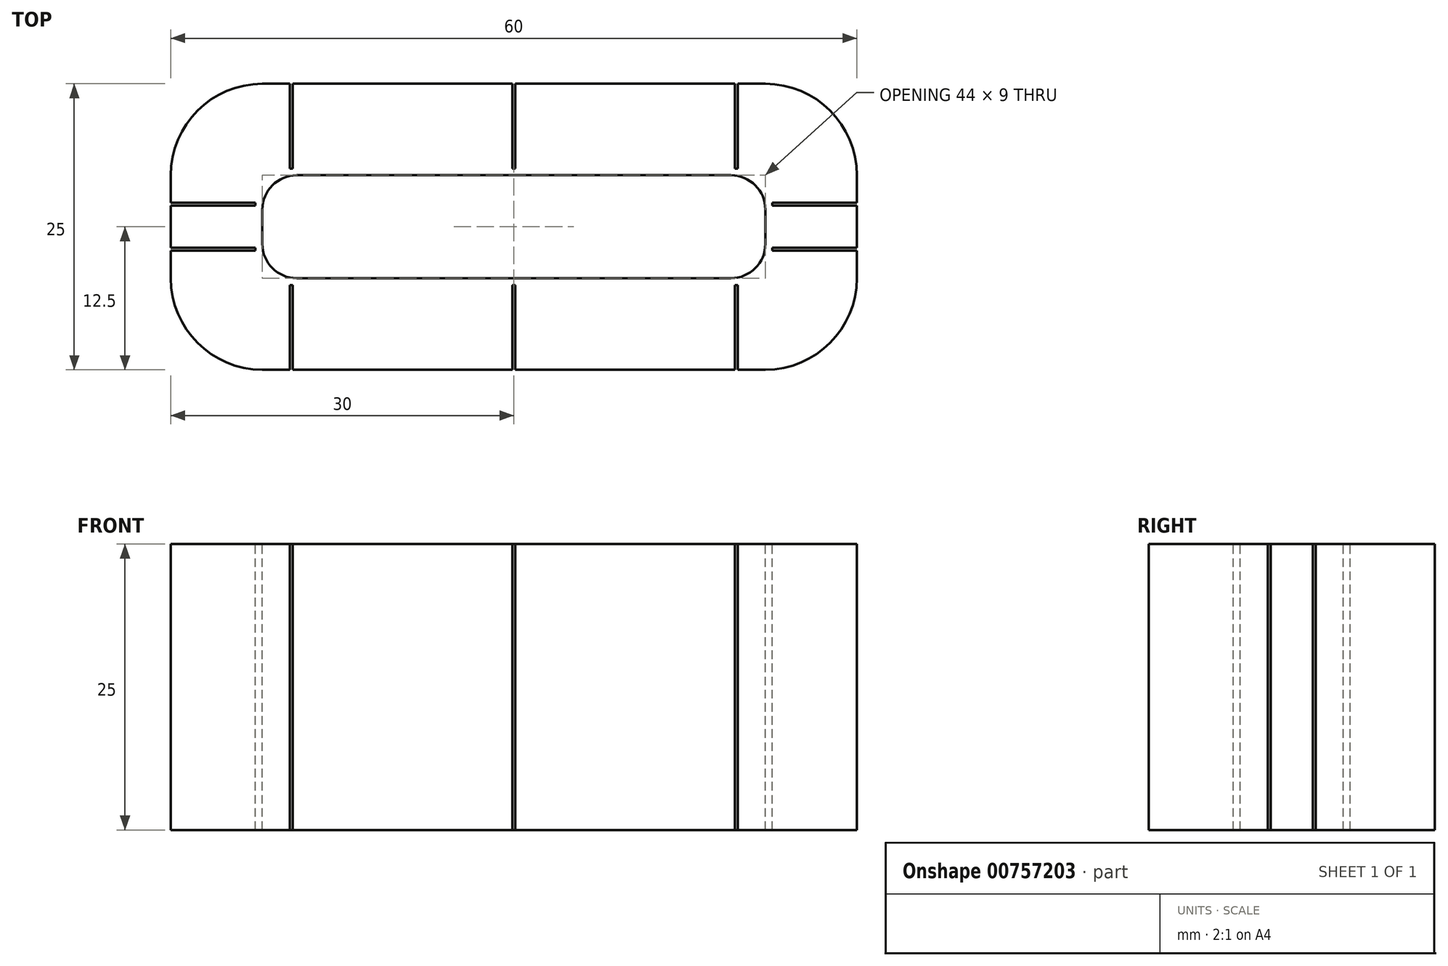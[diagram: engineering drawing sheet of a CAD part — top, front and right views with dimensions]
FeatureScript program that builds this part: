
annotation { "Feature Type Name" : "Feature", "Feature Type Description" : "" }
export const myFeature = defineFeature(function(context is Context, id is Id, definition is map)
    precondition{}
    {
        {
            var Q0;
            Q0=qCreatedBy(makeId("Top.planeOp"),FACE);
            var sketch = newSketch(context, id + "F0", { "sketchPlane" : qUnion([Q0])});
            skLineSegment(sketch, "E0.bottom", {"start": v(22, 12.5) * mm, "end": v(-22, 12.5) * mm});
            skLineSegment(sketch, "E0.top", {"start": v(22, -12.5) * mm, "end": v(-22, -12.5) * mm});
            skLineSegment(sketch, "E0.left", {"start": v(30, 4.5) * mm, "end": v(30, -4.5) * mm});
            skLineSegment(sketch, "E0.right", {"start": v(-30, 4.5) * mm, "end": v(-30, -4.5) * mm});
            skPoint(sketch, "E0.middle", {"position": v(0, 0) * mm});
            skPoint(sketch, "E1.visualSharp", {"position": v(-30, 12.5) * mm});
            skArc(sketch, "E1.filletArc", {"start": v(-22, 12.5) * mm, "mid": v(-27.66, 10.16) * mm, "end": v(-30, 4.5) * mm});
            skPoint(sketch, "E2.visualSharp", {"position": v(30, 12.5) * mm});
            skArc(sketch, "E2.filletArc", {"start": v(30, 4.5) * mm, "mid": v(27.66, 10.16) * mm, "end": v(22, 12.5) * mm});
            skPoint(sketch, "E3.visualSharp", {"position": v(30, -12.5) * mm});
            skArc(sketch, "E3.filletArc", {"start": v(22, -12.5) * mm, "mid": v(27.66, -10.16) * mm, "end": v(30, -4.5) * mm});
            skPoint(sketch, "E4.visualSharp", {"position": v(-30, -12.5) * mm});
            skArc(sketch, "E4.filletArc", {"start": v(-30, -4.5) * mm, "mid": v(-27.66, -10.16) * mm, "end": v(-22, -12.5) * mm});
            skSolve(sketch);
        }
        {
            var Q0;
            Q0 = qSketchRegion(id + "F0", true);
            extrude(context, id + "F1", {"entities" : qUnion([Q0]), "depth" : 25 * mm, "offsetDistance" : 25 * mm});
        }
        {
            var Q0;
            Q0=makeQuery(id+"F1.opExtrude","CAP_FACE",FACE,{"disambiguationData":[OSD([sQuery(id+"F0.wireOp",EDGE,"E0.bottom"),sQuery(id+"F0.wireOp",EDGE,"E0.top"),sQuery(id+"F0.wireOp",EDGE,"E0.left"),sQuery(id+"F0.wireOp",EDGE,"E0.right"),sQuery(id+"F0.wireOp",EDGE,"E1.filletArc"),sQuery(id+"F0.wireOp",EDGE,"E2.filletArc"),sQuery(id+"F0.wireOp",EDGE,"E3.filletArc"),sQuery(id+"F0.wireOp",EDGE,"E4.filletArc")])],"isStart":false});
            var sketch = newSketch(context, id + "F2", { "sketchPlane" : qUnion([Q0])});
            skLineSegment(sketch, "E5.bottom", {"start": v(19, 4.5) * mm, "end": v(-19, 4.5) * mm});
            skLineSegment(sketch, "E5.top", {"start": v(19, -4.5) * mm, "end": v(-19, -4.5) * mm});
            skLineSegment(sketch, "E5.left", {"start": v(22, 1.5) * mm, "end": v(22, -1.5) * mm});
            skLineSegment(sketch, "E5.right", {"start": v(-22, 1.5) * mm, "end": v(-22, -1.5) * mm});
            skPoint(sketch, "E5.middle", {"position": v(0, 0) * mm});
            skPoint(sketch, "E6.visualSharp", {"position": v(-22, 4.5) * mm});
            skArc(sketch, "E6.filletArc", {"start": v(-19, 4.5) * mm, "mid": v(-21.12, 3.62) * mm, "end": v(-22, 1.5) * mm});
            skPoint(sketch, "E7.visualSharp", {"position": v(22, 4.5) * mm});
            skArc(sketch, "E7.filletArc", {"start": v(22, 1.5) * mm, "mid": v(21.12, 3.62) * mm, "end": v(19, 4.5) * mm});
            skPoint(sketch, "E8.visualSharp", {"position": v(-22, -4.5) * mm});
            skArc(sketch, "E8.filletArc", {"start": v(-22, -1.5) * mm, "mid": v(-21.12, -3.62) * mm, "end": v(-19, -4.5) * mm});
            skPoint(sketch, "E9.visualSharp", {"position": v(22, -4.5) * mm});
            skArc(sketch, "E9.filletArc", {"start": v(19, -4.5) * mm, "mid": v(21.12, -3.62) * mm, "end": v(22, -1.5) * mm});
            skSolve(sketch);
        }
        {
            var Q0;
            Q0 = qSketchRegion(id + "F2", true);
            extrude(context, id + "F3", {"entities" : qUnion([Q0]), "operationType" : NewBodyOperationType.ADD, "depth" : 25 * mm, "offsetDistance" : 25 * mm});
        }
        {
            var Q0;
            Q0=makeQuery(id+"F3.opExtrude","CAP_FACE",FACE,{"disambiguationData":[OSD([sQuery(id+"F2.wireOp",EDGE,"E5.bottom"),sQuery(id+"F2.wireOp",EDGE,"E5.top"),sQuery(id+"F2.wireOp",EDGE,"E5.left"),sQuery(id+"F2.wireOp",EDGE,"E5.right"),sQuery(id+"F2.wireOp",EDGE,"E6.filletArc"),sQuery(id+"F2.wireOp",EDGE,"E7.filletArc"),sQuery(id+"F2.wireOp",EDGE,"E8.filletArc"),sQuery(id+"F2.wireOp",EDGE,"E9.filletArc")])],"isStart":false});
            extrude(context, id + "F4", {"entities" : qUnion([Q0]), "operationType" : NewBodyOperationType.REMOVE, "endBound" : BoundingType.THROUGH_ALL, "oppositeDirection" : true, "depth" : 25 * mm, "offsetDistance" : 25 * mm});
        }
        {
            var Q0;
            Q0=makeQuery(id+"F1.opExtrude","CAP_FACE",FACE,{"disambiguationData":[OSD([sQuery(id+"F0.wireOp",EDGE,"E0.bottom"),sQuery(id+"F0.wireOp",EDGE,"E0.top"),sQuery(id+"F0.wireOp",EDGE,"E0.left"),sQuery(id+"F0.wireOp",EDGE,"E0.right"),sQuery(id+"F0.wireOp",EDGE,"E1.filletArc"),sQuery(id+"F0.wireOp",EDGE,"E2.filletArc"),sQuery(id+"F0.wireOp",EDGE,"E3.filletArc"),sQuery(id+"F0.wireOp",EDGE,"E4.filletArc")])],"isStart":false});
            var sketch = newSketch(context, id + "F5", { "sketchPlane" : qUnion([Q0])});
            skLineSegment(sketch, "E10.bottom", {"start": v(19.6, 5.1) * mm, "end": v(-19.6, 5.1) * mm, "construction": true});
            skLineSegment(sketch, "E10.top", {"start": v(19.6, -5.1) * mm, "end": v(-19.6, -5.1) * mm, "construction": true});
            skLineSegment(sketch, "E10.left", {"start": v(22.6, 2.1) * mm, "end": v(22.6, -2.1) * mm, "construction": true});
            skLineSegment(sketch, "E10.right", {"start": v(-22.6, 2.1) * mm, "end": v(-22.6, -2.1) * mm, "construction": true});
            skPoint(sketch, "E10.middle", {"position": v(0, 0) * mm});
            skPoint(sketch, "E11.visualSharp", {"position": v(-22.6, 5.1) * mm});
            skArc(sketch, "E11.filletArc", {"start": v(-19.6, 5.1) * mm, "mid": v(-21.72, 4.22) * mm, "end": v(-22.6, 2.1) * mm, "construction": true});
            skPoint(sketch, "E12.visualSharp", {"position": v(22.6, 5.1) * mm});
            skArc(sketch, "E12.filletArc", {"start": v(22.6, 2.1) * mm, "mid": v(21.72, 4.22) * mm, "end": v(19.6, 5.1) * mm, "construction": true});
            skPoint(sketch, "E13.visualSharp", {"position": v(22.6, -5.1) * mm});
            skArc(sketch, "E13.filletArc", {"start": v(19.6, -5.1) * mm, "mid": v(21.72, -4.22) * mm, "end": v(22.6, -2.1) * mm, "construction": true});
            skPoint(sketch, "E14.visualSharp", {"position": v(-22.6, -5.1) * mm});
            skArc(sketch, "E14.filletArc", {"start": v(-22.6, -2.1) * mm, "mid": v(-21.72, -4.22) * mm, "end": v(-19.6, -5.1) * mm, "construction": true});
            skLineSegment(sketch, "E15.bottom", {"start": v(-19.6, 5.1) * mm, "end": v(-19.35, 5.1) * mm});
            skLineSegment(sketch, "E15.top", {"start": v(-19.6, 12.5) * mm, "end": v(-19.35, 12.5) * mm});
            skLineSegment(sketch, "E15.left", {"start": v(-19.6, 5.1) * mm, "end": v(-19.6, 12.5) * mm});
            skLineSegment(sketch, "E15.right", {"start": v(-19.35, 5.1) * mm, "end": v(-19.35, 12.5) * mm});
            skLineSegment(sketch, "E16.bottom", {"start": v(19.6, 5.1) * mm, "end": v(19.35, 5.1) * mm});
            skLineSegment(sketch, "E16.top", {"start": v(19.6, 12.5) * mm, "end": v(19.35, 12.5) * mm});
            skLineSegment(sketch, "E16.left", {"start": v(19.6, 5.1) * mm, "end": v(19.6, 12.5) * mm});
            skLineSegment(sketch, "E16.right", {"start": v(19.35, 5.1) * mm, "end": v(19.35, 12.5) * mm});
            skLineSegment(sketch, "E17.bottom", {"start": v(-19.6, -5.1) * mm, "end": v(-19.35, -5.1) * mm});
            skLineSegment(sketch, "E17.top", {"start": v(-19.6, -12.5) * mm, "end": v(-19.35, -12.5) * mm});
            skLineSegment(sketch, "E17.left", {"start": v(-19.6, -5.1) * mm, "end": v(-19.6, -12.5) * mm});
            skLineSegment(sketch, "E17.right", {"start": v(-19.35, -5.1) * mm, "end": v(-19.35, -12.5) * mm});
            skLineSegment(sketch, "E18.bottom", {"start": v(19.6, -5.1) * mm, "end": v(19.35, -5.1) * mm});
            skLineSegment(sketch, "E18.top", {"start": v(19.6, -12.5) * mm, "end": v(19.35, -12.5) * mm});
            skLineSegment(sketch, "E18.left", {"start": v(19.6, -5.1) * mm, "end": v(19.6, -12.5) * mm});
            skLineSegment(sketch, "E18.right", {"start": v(19.35, -5.1) * mm, "end": v(19.35, -12.5) * mm});
            skLineSegment(sketch, "E19.bottom", {"start": v(22.6, -2.1) * mm, "end": v(30, -2.1) * mm});
            skLineSegment(sketch, "E19.top", {"start": v(22.6, -1.85) * mm, "end": v(30, -1.85) * mm});
            skLineSegment(sketch, "E19.left", {"start": v(22.6, -2.1) * mm, "end": v(22.6, -1.85) * mm});
            skLineSegment(sketch, "E19.right", {"start": v(30, -2.1) * mm, "end": v(30, -1.85) * mm});
            skLineSegment(sketch, "E20.bottom", {"start": v(22.6, 2.1) * mm, "end": v(30, 2.1) * mm});
            skLineSegment(sketch, "E20.top", {"start": v(22.6, 1.85) * mm, "end": v(30, 1.85) * mm});
            skLineSegment(sketch, "E20.left", {"start": v(22.6, 2.1) * mm, "end": v(22.6, 1.85) * mm});
            skLineSegment(sketch, "E20.right", {"start": v(30, 2.1) * mm, "end": v(30, 1.85) * mm});
            skLineSegment(sketch, "E21.bottom", {"start": v(-22.6, 2.1) * mm, "end": v(-30, 2.1) * mm});
            skLineSegment(sketch, "E21.top", {"start": v(-22.6, 1.85) * mm, "end": v(-30, 1.85) * mm});
            skLineSegment(sketch, "E21.left", {"start": v(-22.6, 2.1) * mm, "end": v(-22.6, 1.85) * mm});
            skLineSegment(sketch, "E21.right", {"start": v(-30, 2.1) * mm, "end": v(-30, 1.85) * mm});
            skLineSegment(sketch, "E22.bottom", {"start": v(-22.6, -2.1) * mm, "end": v(-30, -2.1) * mm});
            skLineSegment(sketch, "E22.top", {"start": v(-22.6, -1.85) * mm, "end": v(-30, -1.85) * mm});
            skLineSegment(sketch, "E22.left", {"start": v(-22.6, -2.1) * mm, "end": v(-22.6, -1.85) * mm});
            skLineSegment(sketch, "E22.right", {"start": v(-30, -2.1) * mm, "end": v(-30, -1.85) * mm});
            skLineSegment(sketch, "E23", {"start": v(0, 0) * mm, "end": v(0, 12.5) * mm, "construction": true});
            skLineSegment(sketch, "E24", {"start": v(0, 12.5) * mm, "end": v(0, -12.5) * mm, "construction": true});
            skLineSegment(sketch, "E25.bottom", {"start": v(-0.12, -12.5) * mm, "end": v(0.13, -12.5) * mm});
            skLineSegment(sketch, "E25.top", {"start": v(-0.13, -5.1) * mm, "end": v(0.12, -5.1) * mm});
            skLineSegment(sketch, "E25.left", {"start": v(-0.12, -12.5) * mm, "end": v(-0.12, -5.1) * mm});
            skLineSegment(sketch, "E25.right", {"start": v(0.13, -12.5) * mm, "end": v(0.13, -5.1) * mm});
            skLineSegment(sketch, "E26.bottom", {"start": v(-0.12, 12.5) * mm, "end": v(0.12, 12.5) * mm});
            skLineSegment(sketch, "E26.top", {"start": v(-0.13, 5.1) * mm, "end": v(0.12, 5.1) * mm});
            skLineSegment(sketch, "E26.left", {"start": v(-0.12, 12.5) * mm, "end": v(-0.12, 5.1) * mm});
            skLineSegment(sketch, "E26.right", {"start": v(0.12, 12.5) * mm, "end": v(0.13, 5.1) * mm});
            skSolve(sketch);
        }
        {
            var Q0;
            Q0 = qSketchRegion(id + "F5", true);
            extrude(context, id + "F6", {"entities" : qUnion([Q0]), "operationType" : NewBodyOperationType.REMOVE, "endBound" : BoundingType.THROUGH_ALL, "oppositeDirection" : true, "depth" : 25 * mm, "offsetDistance" : 25 * mm});
        }
    });
